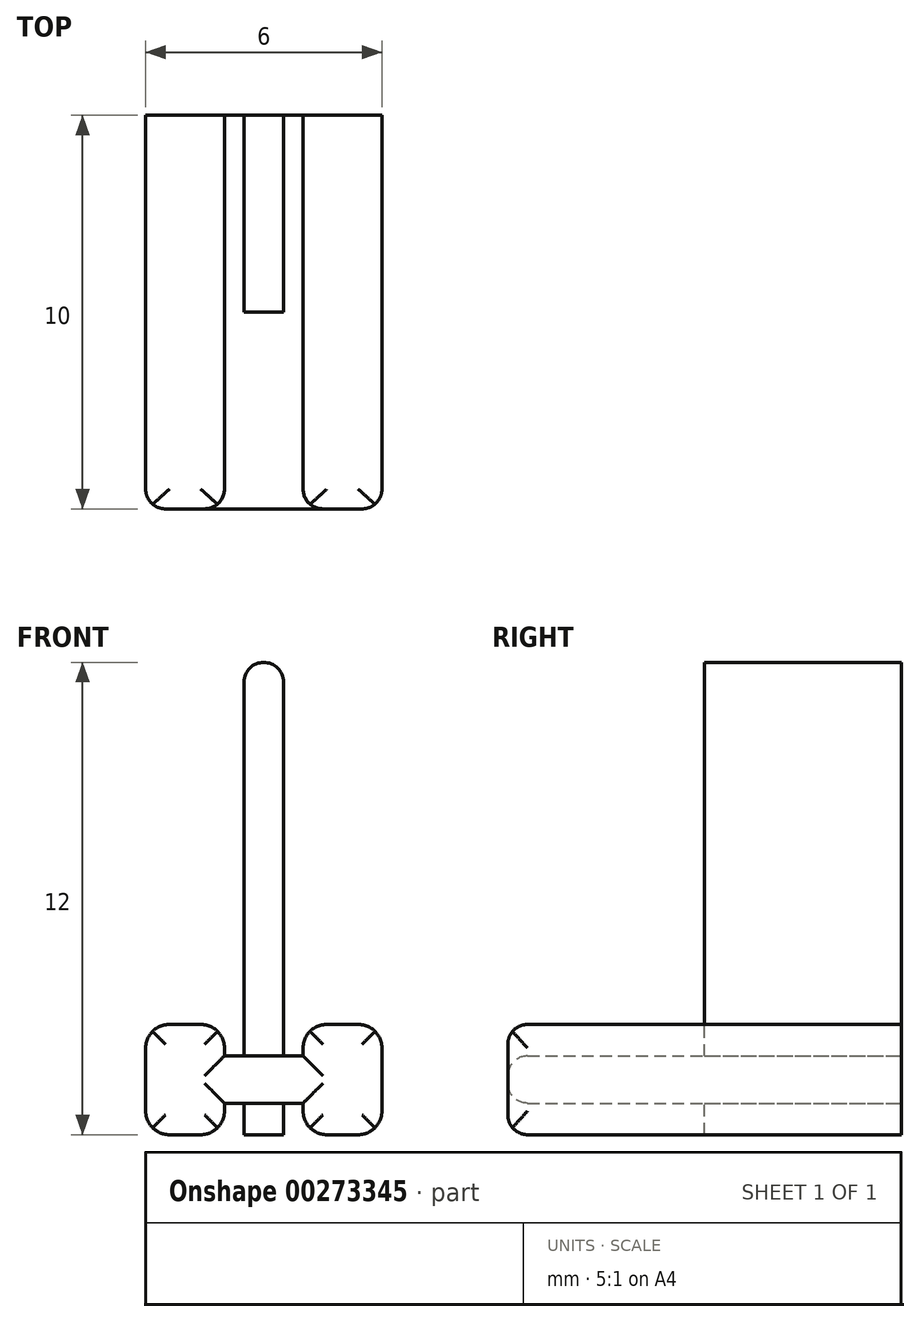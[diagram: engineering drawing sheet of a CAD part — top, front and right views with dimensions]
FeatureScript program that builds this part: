
annotation { "Feature Type Name" : "Feature", "Feature Type Description" : "" }
export const myFeature = defineFeature(function(context is Context, id is Id, definition is map)
    precondition{}
    {
        {
            var Q0;
            Q0=qCreatedBy(makeId("Front.planeOp"),FACE);
            var sketch = newSketch(context, id + "F0", { "sketchPlane" : qUnion([Q0])});
            skLineSegment(sketch, "E0.bottom", {"start": v(2.5, 0.6) * mm, "end": v(-2.5, 0.6) * mm});
            skLineSegment(sketch, "E0.top", {"start": v(2.5, -0.6) * mm, "end": v(-2.5, -0.6) * mm});
            skLineSegment(sketch, "E0.left", {"start": v(2.5, 0.6) * mm, "end": v(2.5, -0.6) * mm});
            skLineSegment(sketch, "E0.right", {"start": v(-2.5, 0.6) * mm, "end": v(-2.5, -0.6) * mm});
            skPoint(sketch, "E0.middle", {"position": v(0, 0) * mm});
            skLineSegment(sketch, "E1", {"start": v(0, 0) * mm, "end": v(-2, 0) * mm, "construction": true});
            skPoint(sketch, "E1.endSnap0", {"position": v(-2.5, 0) * mm});
            skLineSegment(sketch, "E2", {"start": v(0, 0) * mm, "end": v(2, 0) * mm, "construction": true});
            skLineSegment(sketch, "E3.bottom", {"start": v(-1, 1.4) * mm, "end": v(-3, 1.4) * mm});
            skLineSegment(sketch, "E3.top", {"start": v(-1, -1.4) * mm, "end": v(-3, -1.4) * mm});
            skLineSegment(sketch, "E3.left", {"start": v(-1, 1.4) * mm, "end": v(-1, -1.4) * mm});
            skLineSegment(sketch, "E3.right", {"start": v(-3, 1.4) * mm, "end": v(-3, -1.4) * mm});
            skPoint(sketch, "E3.middle", {"position": v(-2, 0) * mm});
            skPoint(sketch, "E4.middle", {"position": v(2, 0) * mm});
            skPoint(sketch, "E4.cornerSnap0", {"position": v(2.5, 0) * mm});
            skLineSegment(sketch, "E5.bottom", {"start": v(3, 1.4) * mm, "end": v(1, 1.4) * mm});
            skLineSegment(sketch, "E5.top", {"start": v(3, -1.4) * mm, "end": v(1, -1.4) * mm});
            skLineSegment(sketch, "E5.left", {"start": v(3, 1.4) * mm, "end": v(3, -1.4) * mm});
            skLineSegment(sketch, "E5.right", {"start": v(1, 1.4) * mm, "end": v(1, -1.4) * mm});
            skLineSegment(sketch, "E6", {"start": v(-1, -1.4) * mm, "end": v(1, -1.4) * mm, "construction": true});
            skLineSegment(sketch, "E7", {"start": v(1, -1.4) * mm, "end": v(0.5, -1.4) * mm, "construction": true});
            skLineSegment(sketch, "E8.bottom", {"start": v(0.5, -1.4) * mm, "end": v(-0.5, -1.4) * mm});
            skLineSegment(sketch, "E8.top", {"start": v(0.5, 10.6) * mm, "end": v(-0.5, 10.6) * mm});
            skLineSegment(sketch, "E8.left", {"start": v(0.5, -1.4) * mm, "end": v(0.5, 10.6) * mm});
            skLineSegment(sketch, "E8.right", {"start": v(-0.5, -1.4) * mm, "end": v(-0.5, 10.6) * mm});
            skSolve(sketch);
        }
        {
            var Q0;
            {var subQ1=sQuery(id+"F0.wireOp",EDGE,"E0.left");Q0=makeQuery(id+"F0.imprint","IMPRINT",FACE,{"disambiguationData":[TD([[makeQuery(id+"F0.imprint","IMPRINT",EDGE,{"derivedFrom":subQ1}),1.0]])]});}
            var Q1;
            {var subQ1=sQuery(id+"F0.wireOp",EDGE,"E0.right");Q1=makeQuery(id+"F0.imprint","IMPRINT",FACE,{"disambiguationData":[TD([[makeQuery(id+"F0.imprint","IMPRINT",EDGE,{"derivedFrom":subQ1}),-1.0]])]});}
            var Q2;
            {var subQ0=sQuery(id+"F0.wireOp",EDGE,"E0.left");Q2=makeQuery(id+"F0.imprint","IMPRINT",FACE,{"disambiguationData":[TD([[makeQuery(id+"F0.imprint","IMPRINT",EDGE,{"derivedFrom":subQ0}),-1.0]])]});}
            var Q3;
            {var subQ0=sQuery(id+"F0.wireOp",EDGE,"E5.right");var subQ1=sQuery(id+"F0.wireOp",EDGE,"E0.bottom");var subQ2=makeQuery(id+"F0.imprint","INTERSECT",VERTEX,{"derivedFrom":[subQ1,subQ0]});Q3=makeQuery(id+"F0.imprint","IMPRINT",FACE,{"disambiguationData":[TD([[makeQuery(id+"F0.imprint","IMPRINT",EDGE,{"disambiguationData":[TD([[subQ2,-1.0]])],"derivedFrom":subQ1}),1.0]])]});}
            var Q4;
            {var subQ0=sQuery(id+"F0.wireOp",EDGE,"E8.right");var subQ1=sQuery(id+"F0.wireOp",EDGE,"E0.bottom");var subQ2=makeQuery(id+"F0.imprint","INTERSECT",VERTEX,{"derivedFrom":[subQ1,subQ0]});Q4=makeQuery(id+"F0.imprint","IMPRINT",FACE,{"disambiguationData":[TD([[makeQuery(id+"F0.imprint","IMPRINT",EDGE,{"disambiguationData":[TD([[subQ2,-1.0]])],"derivedFrom":subQ1}),1.0]])]});}
            var Q5;
            {var subQ0=sQuery(id+"F0.wireOp",EDGE,"E0.right");Q5=makeQuery(id+"F0.imprint","IMPRINT",FACE,{"disambiguationData":[TD([[makeQuery(id+"F0.imprint","IMPRINT",EDGE,{"derivedFrom":subQ0}),1.0]])]});}
            var Q6;
            {var subQ0=sQuery(id+"F0.wireOp",EDGE,"E8.left");var subQ1=sQuery(id+"F0.wireOp",EDGE,"E0.bottom");var subQ2=makeQuery(id+"F0.imprint","INTERSECT",VERTEX,{"derivedFrom":[subQ1,subQ0]});Q6=makeQuery(id+"F0.imprint","IMPRINT",FACE,{"disambiguationData":[TD([[makeQuery(id+"F0.imprint","IMPRINT",EDGE,{"disambiguationData":[TD([[subQ2,-1.0]])],"derivedFrom":subQ1}),1.0]])]});}
            extrude(context, id + "F1", {"entities" : qUnion([Q0, Q1, Q2, Q3, Q4, Q5, Q6]), "depth" : 10 * mm});
        }
        {
            var Q0;
            {var subQ5=sQuery(id+"F0.wireOp",EDGE,"E8.top");Q0=makeQuery(id+"F0.imprint","IMPRINT",FACE,{"disambiguationData":[TD([[makeQuery(id+"F0.imprint","IMPRINT",EDGE,{"derivedFrom":subQ5}),1.0]])]});}
            var Q1;
            {var subQ5=sQuery(id+"F0.wireOp",EDGE,"E8.bottom");Q1=makeQuery(id+"F0.imprint","IMPRINT",FACE,{"disambiguationData":[TD([[makeQuery(id+"F0.imprint","IMPRINT",EDGE,{"derivedFrom":subQ5}),-1.0]])]});}
            extrude(context, id + "F2", {"entities" : qUnion([Q0, Q1]), "operationType" : NewBodyOperationType.ADD, "depth" : 5 * mm});
        }
        {
            var Q0;
            Q0=makeQuery(id+"F2.opExtrude","SWEPT_EDGE",EDGE,{"disambiguationData":[OSD([sQuery(id+"F0.wireOp",EDGE,"E8.top"),sQuery(id+"F0.wireOp",EDGE,"E8.left")])]});
            var Q1;
            Q1=makeQuery(id+"F2.opExtrude","SWEPT_EDGE",EDGE,{"disambiguationData":[OSD([sQuery(id+"F0.wireOp",EDGE,"E8.top"),sQuery(id+"F0.wireOp",EDGE,"E8.right")])]});
            fillet(context, id + "F3", {"entities" : qUnion([Q0, Q1]), "radius" : .5 * mm, "tangentPropagation" : true, "allowEdgeOverflow" : false});
        }
        {
            var Q0;
            Q0=makeQuery(id+"F1.opExtrude","CAP_FACE",FACE,{"disambiguationData":[OSD([sQuery(id+"F0.wireOp",EDGE,"E0.bottom"),sQuery(id+"F0.wireOp",EDGE,"E0.top"),sQuery(id+"F0.wireOp",EDGE,"E3.bottom"),sQuery(id+"F0.wireOp",EDGE,"E3.top"),sQuery(id+"F0.wireOp",EDGE,"E3.left"),sQuery(id+"F0.wireOp",EDGE,"E3.right"),sQuery(id+"F0.wireOp",EDGE,"E5.bottom"),sQuery(id+"F0.wireOp",EDGE,"E5.top"),sQuery(id+"F0.wireOp",EDGE,"E5.left"),sQuery(id+"F0.wireOp",EDGE,"E5.right")])],"isStart":false});
            fillet(context, id + "F4", {"entities" : qUnion([Q0]), "radius" : .5 * mm, "tangentPropagation" : true, "allowEdgeOverflow" : false});
        }
        {
            var Q0;
            Q0=makeQuery(id+"F1.opExtrude","SWEPT_EDGE",EDGE,{"disambiguationData":[OSD([sQuery(id+"F0.wireOp",EDGE,"E3.bottom"),sQuery(id+"F0.wireOp",EDGE,"E3.right")])]});
            var Q1;
            Q1=makeQuery(id+"F1.opExtrude","SWEPT_EDGE",EDGE,{"disambiguationData":[OSD([sQuery(id+"F0.wireOp",EDGE,"E3.bottom"),sQuery(id+"F0.wireOp",EDGE,"E3.left")])]});
            var Q2;
            Q2=makeQuery(id+"F1.opExtrude","SWEPT_EDGE",EDGE,{"disambiguationData":[OSD([sQuery(id+"F0.wireOp",EDGE,"E5.bottom"),sQuery(id+"F0.wireOp",EDGE,"E5.right")])]});
            var Q3;
            Q3=makeQuery(id+"F1.opExtrude","SWEPT_EDGE",EDGE,{"disambiguationData":[OSD([sQuery(id+"F0.wireOp",EDGE,"E5.bottom"),sQuery(id+"F0.wireOp",EDGE,"E5.left")])]});
            var Q4;
            Q4=makeQuery(id+"F1.opExtrude","SWEPT_EDGE",EDGE,{"disambiguationData":[OSD([sQuery(id+"F0.wireOp",EDGE,"E3.top"),sQuery(id+"F0.wireOp",EDGE,"E3.right")])]});
            var Q5;
            Q5=makeQuery(id+"F1.opExtrude","SWEPT_EDGE",EDGE,{"disambiguationData":[OSD([sQuery(id+"F0.wireOp",EDGE,"E3.top"),sQuery(id+"F0.wireOp",EDGE,"E3.left")])]});
            var Q6;
            Q6=makeQuery(id+"F1.opExtrude","SWEPT_EDGE",EDGE,{"disambiguationData":[OSD([sQuery(id+"F0.wireOp",EDGE,"E5.top"),sQuery(id+"F0.wireOp",EDGE,"E5.right")])]});
            var Q7;
            Q7=makeQuery(id+"F1.opExtrude","SWEPT_EDGE",EDGE,{"disambiguationData":[OSD([sQuery(id+"F0.wireOp",EDGE,"E5.top"),sQuery(id+"F0.wireOp",EDGE,"E5.left")])]});
            fillet(context, id + "F5", {"entities" : qUnion([Q0, Q1, Q2, Q3, Q4, Q5, Q6, Q7]), "radius" : .6 * mm, "allowEdgeOverflow" : false});
        }
    });
